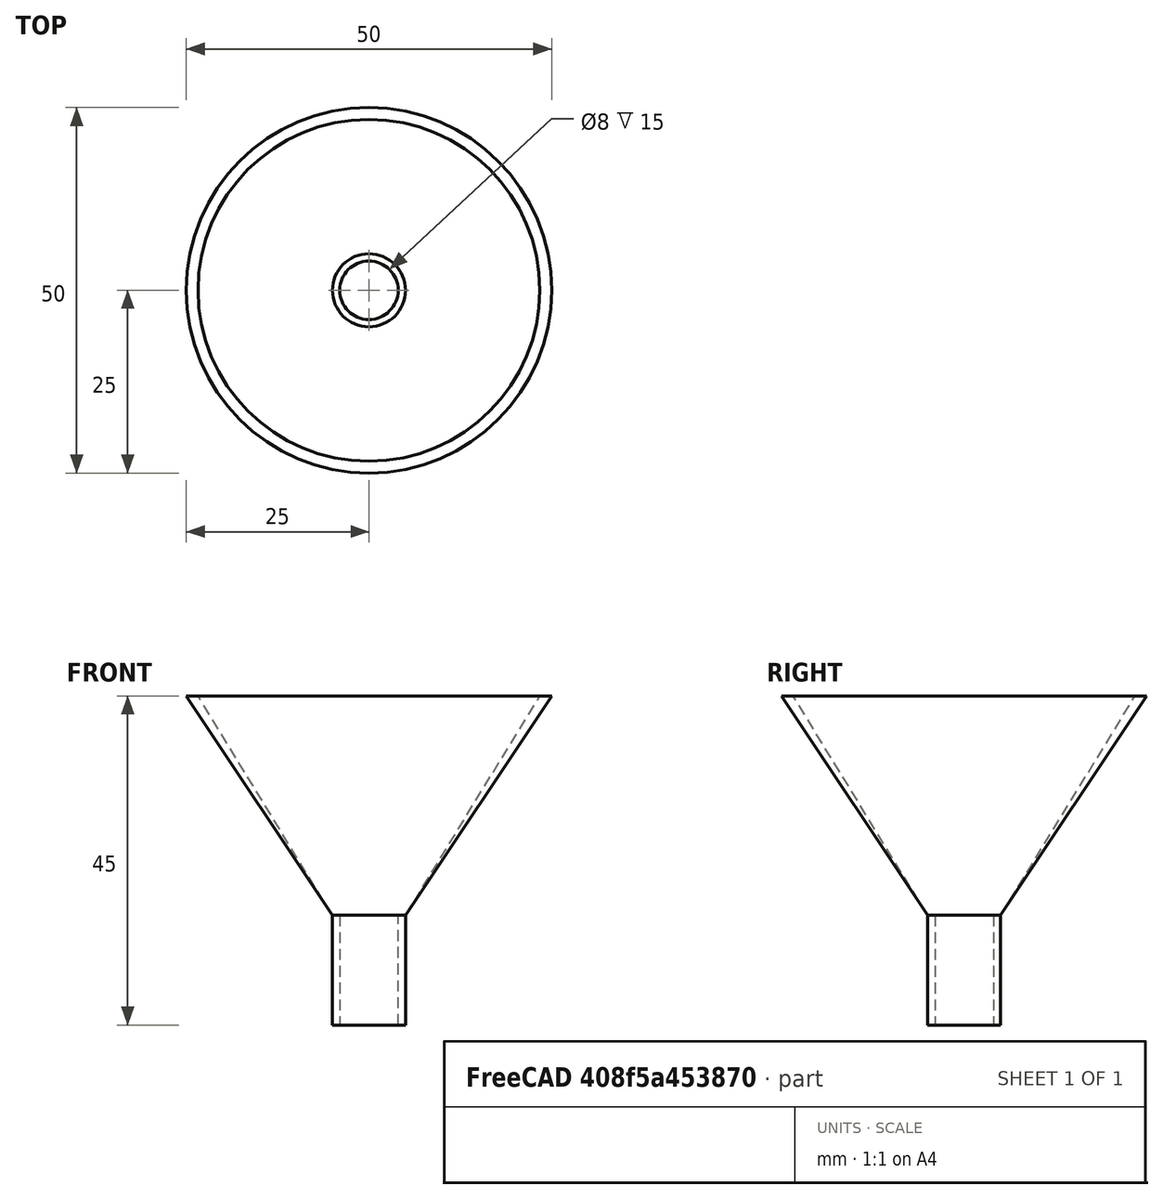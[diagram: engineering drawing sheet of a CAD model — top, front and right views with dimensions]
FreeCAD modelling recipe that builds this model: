
FCSTD DOCUMENT  (FreeCAD 0.21R33694 (Git))
Label: OJT1_T14R03_embut
License: All rights reserved
LicenseURL: https://en.wikipedia.org/wiki/All_rights_reserved
objects: Part::Cylinder×2, Part::Cut×2, Part::Cone×2
note: 6 computed .brp shape members not serialized (recipe doc carries the construction recipe); baked Part::Feature solids carry a one-line shape summary decoded from their .brp

FEATURE [Part::Cylinder] Cylinder  label="Cilindre"
  Angle = 360
  AttacherType = Attacher::AttachEngine3D
  FirstAngle = 0
  Height = 15
  Radius = 5
  SecondAngle = 0
FEATURE [Part::Cylinder] Cylinder001  label="Cilindre001"
  Angle = 360
  AttacherType = Attacher::AttachEngine3D
  FirstAngle = 0
  Height = 17
  Placement = pos=(0,0,-1) rot=(0,0,1;0rad)
  Radius = 4
  SecondAngle = 0
FEATURE [Part::Cut] Cut
  Base = -> Cylinder
  Tool = -> Cylinder001
FEATURE [Part::Cone] Cone  label="Con"
  Angle = 360
  AttacherType = Attacher::AttachEngine3D
  Height = 30
  Placement = pos=(0,0,15) rot=(0,0,1;0rad)
  Radius1 = 5
  Radius2 = 25
FEATURE [Part::Cone] Cone001  label="Con001"
  Angle = 360
  AttacherType = Attacher::AttachEngine3D
  Height = 31
  Placement = pos=(0,0,15) rot=(0,0,1;0rad)
  Radius1 = 5
  Radius2 = 24
FEATURE [Part::Cut] Cut001
  Base = -> Cone
  Tool = -> Cone001
